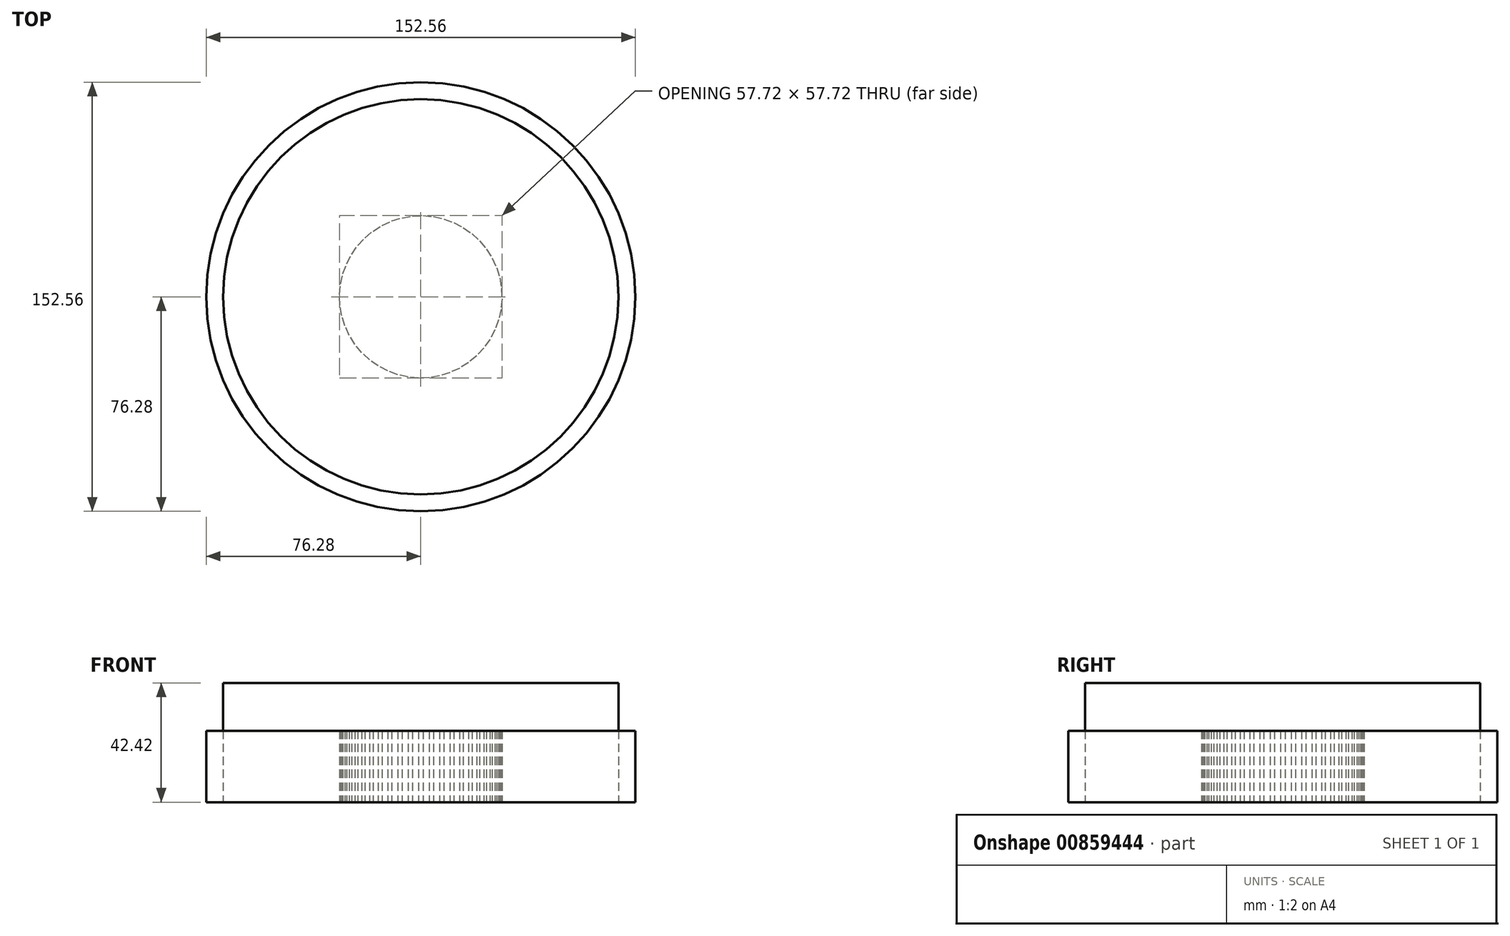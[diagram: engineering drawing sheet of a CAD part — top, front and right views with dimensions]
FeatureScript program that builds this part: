
annotation { "Feature Type Name" : "Feature", "Feature Type Description" : "" }
export const myFeature = defineFeature(function(context is Context, id is Id, definition is map)
    precondition{}
    {
        {
            var Q0;
            Q0=qCreatedBy(makeId("Top.planeOp"),FACE);
            var sketch = newSketch(context, id + "F0", { "sketchPlane" : qUnion([Q0])});
            skCircle(sketch, "E0.cCircle", {"center": v(0, 0) * mm, "radius": 28.8 * mm, "construction": true});
            skLineSegment(sketch, "E0.0", {"start": v(-27.67, 8.23) * mm, "end": v(-26.36, 11.77) * mm});
            skLineSegment(sketch, "E0.1", {"start": v(-26.36, 11.77) * mm, "end": v(-24.6, 15.11) * mm});
            skLineSegment(sketch, "E0.2", {"start": v(-24.6, 15.11) * mm, "end": v(-22.42, 18.2) * mm});
            skLineSegment(sketch, "E0.3", {"start": v(-22.42, 18.2) * mm, "end": v(-19.85, 20.96) * mm});
            skLineSegment(sketch, "E0.4", {"start": v(-19.85, 20.96) * mm, "end": v(-16.94, 23.38) * mm});
            skLineSegment(sketch, "E0.5", {"start": v(-16.94, 23.38) * mm, "end": v(-13.75, 25.39) * mm});
            skLineSegment(sketch, "E0.6", {"start": v(-13.75, 25.39) * mm, "end": v(-10.32, 26.97) * mm});
            skLineSegment(sketch, "E0.7", {"start": v(-10.32, 26.97) * mm, "end": v(-6.7, 28.08) * mm});
            skLineSegment(sketch, "E0.8", {"start": v(-6.7, 28.08) * mm, "end": v(-2.99, 28.72) * mm});
            skLineSegment(sketch, "E0.9", {"start": v(-2.99, 28.72) * mm, "end": v(0.79, 28.86) * mm});
            skLineSegment(sketch, "E0.10", {"start": v(0.79, 28.86) * mm, "end": v(4.55, 28.51) * mm});
            skLineSegment(sketch, "E0.11", {"start": v(4.55, 28.51) * mm, "end": v(8.23, 27.67) * mm});
            skLineSegment(sketch, "E0.12", {"start": v(8.23, 27.67) * mm, "end": v(11.77, 26.36) * mm});
            skLineSegment(sketch, "E0.13", {"start": v(11.77, 26.36) * mm, "end": v(15.11, 24.6) * mm});
            skLineSegment(sketch, "E0.14", {"start": v(15.11, 24.6) * mm, "end": v(18.2, 22.42) * mm});
            skLineSegment(sketch, "E0.15", {"start": v(18.2, 22.42) * mm, "end": v(20.96, 19.85) * mm});
            skLineSegment(sketch, "E0.16", {"start": v(20.96, 19.85) * mm, "end": v(23.38, 16.94) * mm});
            skLineSegment(sketch, "E0.17", {"start": v(23.38, 16.94) * mm, "end": v(25.39, 13.75) * mm});
            skLineSegment(sketch, "E0.18", {"start": v(25.39, 13.75) * mm, "end": v(26.97, 10.32) * mm});
            skLineSegment(sketch, "E0.19", {"start": v(26.97, 10.32) * mm, "end": v(28.08, 6.7) * mm});
            skLineSegment(sketch, "E0.20", {"start": v(28.08, 6.7) * mm, "end": v(28.72, 2.99) * mm});
            skLineSegment(sketch, "E0.21", {"start": v(28.72, 2.99) * mm, "end": v(28.86, -0.79) * mm});
            skLineSegment(sketch, "E0.22", {"start": v(28.86, -0.79) * mm, "end": v(28.51, -4.55) * mm});
            skLineSegment(sketch, "E0.23", {"start": v(28.51, -4.55) * mm, "end": v(27.67, -8.23) * mm});
            skLineSegment(sketch, "E0.24", {"start": v(27.67, -8.23) * mm, "end": v(26.36, -11.77) * mm});
            skLineSegment(sketch, "E0.25", {"start": v(26.36, -11.77) * mm, "end": v(24.6, -15.11) * mm});
            skLineSegment(sketch, "E0.26", {"start": v(24.6, -15.11) * mm, "end": v(22.42, -18.2) * mm});
            skLineSegment(sketch, "E0.27", {"start": v(22.42, -18.2) * mm, "end": v(19.85, -20.96) * mm});
            skLineSegment(sketch, "E0.28", {"start": v(19.85, -20.96) * mm, "end": v(16.94, -23.38) * mm});
            skLineSegment(sketch, "E0.29", {"start": v(16.94, -23.38) * mm, "end": v(13.75, -25.39) * mm});
            skLineSegment(sketch, "E0.30", {"start": v(13.75, -25.39) * mm, "end": v(10.32, -26.97) * mm});
            skLineSegment(sketch, "E0.31", {"start": v(10.32, -26.97) * mm, "end": v(6.7, -28.08) * mm});
            skLineSegment(sketch, "E0.32", {"start": v(6.7, -28.08) * mm, "end": v(2.99, -28.72) * mm});
            skLineSegment(sketch, "E0.33", {"start": v(2.99, -28.72) * mm, "end": v(-0.79, -28.86) * mm});
            skLineSegment(sketch, "E0.34", {"start": v(-0.79, -28.86) * mm, "end": v(-4.55, -28.51) * mm});
            skLineSegment(sketch, "E0.35", {"start": v(-4.55, -28.51) * mm, "end": v(-8.23, -27.67) * mm});
            skLineSegment(sketch, "E0.36", {"start": v(-8.23, -27.67) * mm, "end": v(-11.77, -26.36) * mm});
            skLineSegment(sketch, "E0.37", {"start": v(-11.77, -26.36) * mm, "end": v(-15.11, -24.6) * mm});
            skLineSegment(sketch, "E0.38", {"start": v(-15.11, -24.6) * mm, "end": v(-18.2, -22.42) * mm});
            skLineSegment(sketch, "E0.39", {"start": v(-18.2, -22.42) * mm, "end": v(-20.96, -19.85) * mm});
            skLineSegment(sketch, "E0.40", {"start": v(-20.96, -19.85) * mm, "end": v(-23.38, -16.94) * mm});
            skLineSegment(sketch, "E0.41", {"start": v(-23.38, -16.94) * mm, "end": v(-25.39, -13.75) * mm});
            skLineSegment(sketch, "E0.42", {"start": v(-25.39, -13.75) * mm, "end": v(-26.97, -10.32) * mm});
            skLineSegment(sketch, "E0.43", {"start": v(-26.97, -10.32) * mm, "end": v(-28.08, -6.7) * mm});
            skLineSegment(sketch, "E0.44", {"start": v(-28.08, -6.7) * mm, "end": v(-28.72, -2.99) * mm});
            skLineSegment(sketch, "E0.45", {"start": v(-28.72, -2.99) * mm, "end": v(-28.86, 0.79) * mm});
            skLineSegment(sketch, "E0.46", {"start": v(-28.86, 0.79) * mm, "end": v(-28.51, 4.55) * mm});
            skLineSegment(sketch, "E0.47", {"start": v(-28.51, 4.55) * mm, "end": v(-27.67, 8.23) * mm});
            skPoint(sketch, "E0.0.midPoint", {"position": v(-27.02, 10) * mm});
            skCircle(sketch, "E1", {"center": v(0, 0) * mm, "radius": 76.28 * mm});
            skSolve(sketch);
        }
        {
            var Q0;
            Q0 = qSketchRegion(id + "F0", true);
            extrude(context, id + "F1", {"entities" : qUnion([Q0]), "depth" : 25.4 * mm, "offsetDistance" : 25.4 * mm});
        }
        {
            var Q0;
            Q0=qCreatedBy(makeId("Top.planeOp"),FACE);
            var sketch = newSketch(context, id + "F2", { "sketchPlane" : qUnion([Q0])});
            skCircle(sketch, "E2", {"center": v(0, 0) * mm, "radius": 70.25 * mm});
            skSolve(sketch);
        }
        {
            var Q0;
            Q0 = qSketchRegion(id + "F2", true);
            extrude(context, id + "F3", {"entities" : qUnion([Q0]), "depth" : 42.42 * mm, "offsetDistance" : 25.4 * mm});
        }
    });
